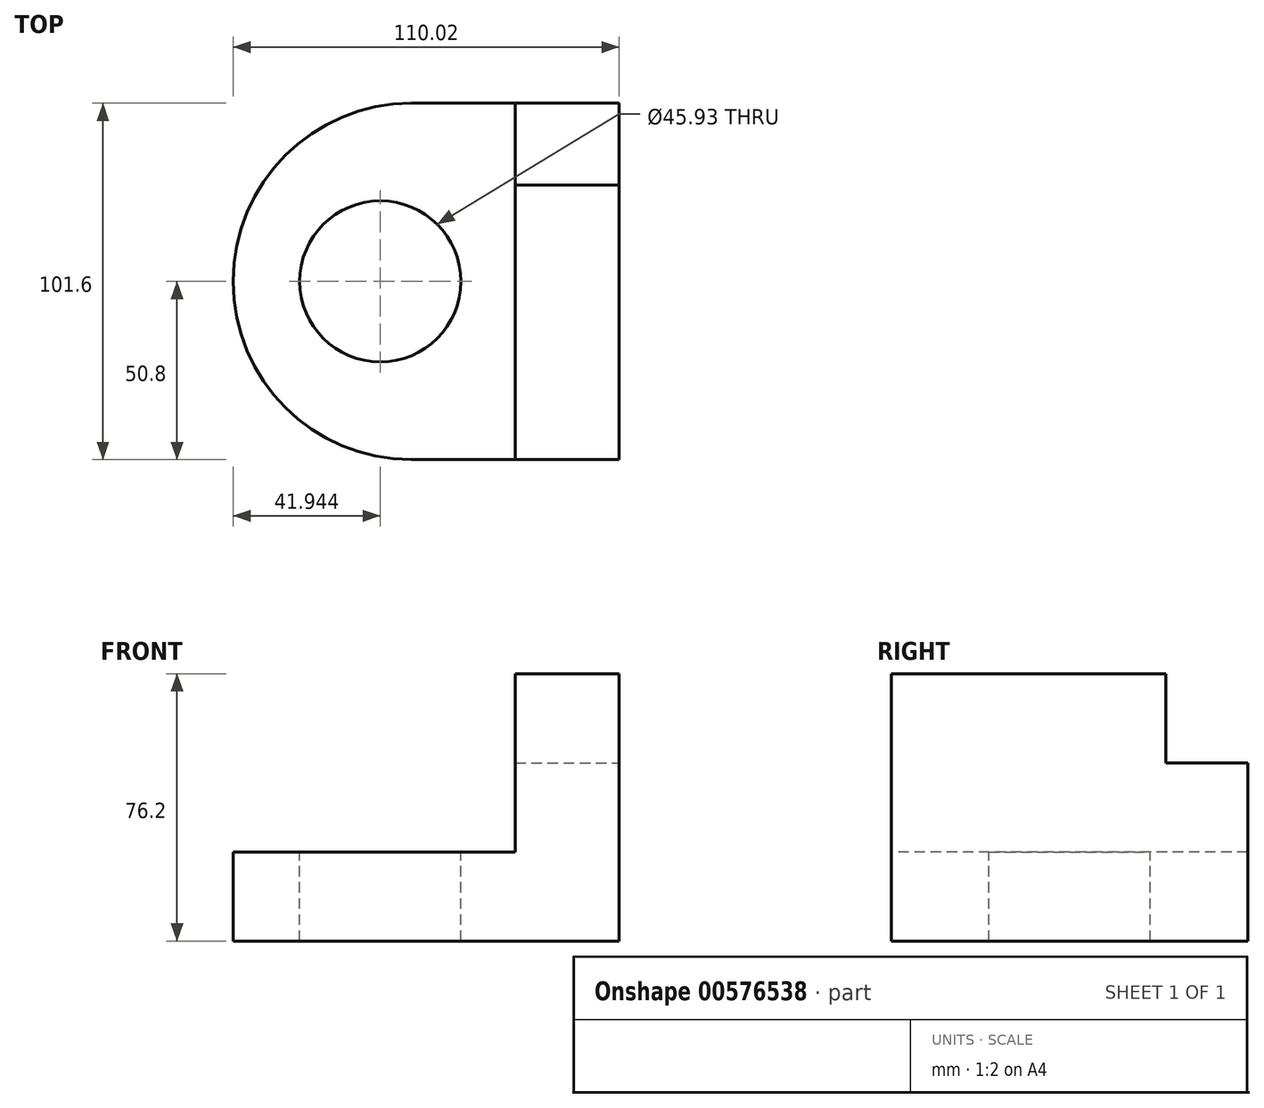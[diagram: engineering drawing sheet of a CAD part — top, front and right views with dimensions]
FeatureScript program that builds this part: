
annotation { "Feature Type Name" : "Feature", "Feature Type Description" : "" }
export const myFeature = defineFeature(function(context is Context, id is Id, definition is map)
    precondition{}
    {
        {
            var Q0;
            Q0=qCreatedBy(makeId("Top.planeOp"),FACE);
            var sketch = newSketch(context, id + "F0", { "sketchPlane" : qUnion([Q0])});
            skLineSegment(sketch, "E0.bottom", {"start": v(55.01, -50.8) * mm, "end": v(-4.21, -50.8) * mm});
            skLineSegment(sketch, "E0.top", {"start": v(55.01, 50.8) * mm, "end": v(-4.21, 50.8) * mm});
            skLineSegment(sketch, "E0.left", {"start": v(55.01, -50.8) * mm, "end": v(55.01, 50.8) * mm});
            skLineSegment(sketch, "E0.right", {"start": v(-55.01, 0) * mm, "end": v(-55.01, 0) * mm});
            skPoint(sketch, "E0.middle", {"position": v(0, 0) * mm});
            skPoint(sketch, "E1.visualSharp", {"position": v(-55.01, 50.8) * mm});
            skArc(sketch, "E1.filletArc", {"start": v(-4.21, 50.8) * mm, "mid": v(-40.13, 35.92) * mm, "end": v(-55.01, 0) * mm});
            skPoint(sketch, "E2.visualSharp", {"position": v(-55.01, -50.8) * mm});
            skArc(sketch, "E2.filletArc", {"start": v(-55.01, 0) * mm, "mid": v(-40.13, -35.92) * mm, "end": v(-4.21, -50.8) * mm});
            skSolve(sketch);
        }
        {
            var Q0;
            Q0 = qSketchRegion(id + "F0", true);
            extrude(context, id + "F1", {"entities" : qUnion([Q0]), "depth" : 25.4 * mm, "offsetDistance" : 25.4 * mm});
        }
        {
            var Q0;
            Q0=makeQuery(id+"F1.opExtrude","CAP_FACE",FACE,{"disambiguationData":[OSD([sQuery(id+"F0.wireOp",EDGE,"E0.bottom"),sQuery(id+"F0.wireOp",EDGE,"E0.top"),sQuery(id+"F0.wireOp",EDGE,"E0.left"),sQuery(id+"F0.wireOp",EDGE,"E1.filletArc"),sQuery(id+"F0.wireOp",EDGE,"E2.filletArc")])],"isStart":false});
            var sketch = newSketch(context, id + "F2", { "sketchPlane" : qUnion([Q0])});
            skCircle(sketch, "E3", {"center": v(-13.07, 0) * mm, "radius": 22.96 * mm});
            skSolve(sketch);
        }
        {
            var Q0;
            Q0=makeQuery(id+"F2.imprint","IMPRINT",FACE,{"disambiguationData":[TD([[makeQuery(id+"F2.imprint","IMPRINT",EDGE,{"derivedFrom":sQuery(id+"F2.wireOp",EDGE,"E3")}),1.0]])]});
            extrude(context, id + "F3", {"entities" : qUnion([Q0]), "operationType" : NewBodyOperationType.REMOVE, "endBound" : BoundingType.THROUGH_ALL, "oppositeDirection" : true, "depth" : 25.4 * mm, "offsetDistance" : 25.4 * mm});
        }
        {
            var Q0;
            Q0=makeQuery(id+"F1.opExtrude","CAP_FACE",FACE,{"disambiguationData":[OSD([sQuery(id+"F0.wireOp",EDGE,"E0.bottom"),sQuery(id+"F0.wireOp",EDGE,"E0.top"),sQuery(id+"F0.wireOp",EDGE,"E0.left"),sQuery(id+"F0.wireOp",EDGE,"E1.filletArc"),sQuery(id+"F0.wireOp",EDGE,"E2.filletArc")])],"isStart":false});
            var sketch = newSketch(context, id + "F4", { "sketchPlane" : qUnion([Q0])});
            skLineSegment(sketch, "E4.bottom", {"start": v(25.4, 50.8) * mm, "end": v(55.01, 50.8) * mm});
            skLineSegment(sketch, "E4.top", {"start": v(25.4, -50.8) * mm, "end": v(55.01, -50.8) * mm});
            skLineSegment(sketch, "E4.left", {"start": v(25.4, 50.8) * mm, "end": v(25.4, -50.8) * mm});
            skLineSegment(sketch, "E4.right", {"start": v(55.01, 50.8) * mm, "end": v(55.01, -50.8) * mm});
            skSolve(sketch);
        }
        {
            var Q0;
            Q0=makeQuery(id+"F4.imprint","IMPRINT",FACE,{"disambiguationData":[TD([[makeQuery(id+"F4.imprint","IMPRINT",EDGE,{"derivedFrom":sQuery(id+"F4.wireOp",EDGE,"E4.bottom")}),1.0]])]});
            extrude(context, id + "F5", {"entities" : qUnion([Q0]), "operationType" : NewBodyOperationType.ADD, "depth" : 25.4 * mm, "offsetDistance" : 25.4 * mm});
        }
        {
            var Q0;
            Q0=makeQuery(id+"F5.opExtrude","CAP_FACE",FACE,{"disambiguationData":[OSD([sQuery(id+"F4.wireOp",EDGE,"E4.bottom"),sQuery(id+"F4.wireOp",EDGE,"E4.top"),sQuery(id+"F4.wireOp",EDGE,"E4.left"),sQuery(id+"F4.wireOp",EDGE,"E4.right")])],"isStart":false});
            var sketch = newSketch(context, id + "F6", { "sketchPlane" : qUnion([Q0])});
            skLineSegment(sketch, "E5.bottom", {"start": v(25.4, 27.5) * mm, "end": v(55.01, 27.5) * mm});
            skLineSegment(sketch, "E5.top", {"start": v(25.4, -50.8) * mm, "end": v(55.01, -50.8) * mm});
            skLineSegment(sketch, "E5.left", {"start": v(25.4, 27.5) * mm, "end": v(25.4, -50.8) * mm});
            skLineSegment(sketch, "E5.right", {"start": v(55.01, 27.5) * mm, "end": v(55.01, -50.8) * mm});
            skSolve(sketch);
        }
        {
            var Q0;
            Q0=makeQuery(id+"F6.imprint","IMPRINT",FACE,{"disambiguationData":[TD([[makeQuery(id+"F6.imprint","IMPRINT",EDGE,{"derivedFrom":sQuery(id+"F6.wireOp",EDGE,"E5.bottom")}),-1.0]])]});
            extrude(context, id + "F7", {"entities" : qUnion([Q0]), "operationType" : NewBodyOperationType.ADD, "depth" : 25.4 * mm, "offsetDistance" : 25.4 * mm});
        }
    });
